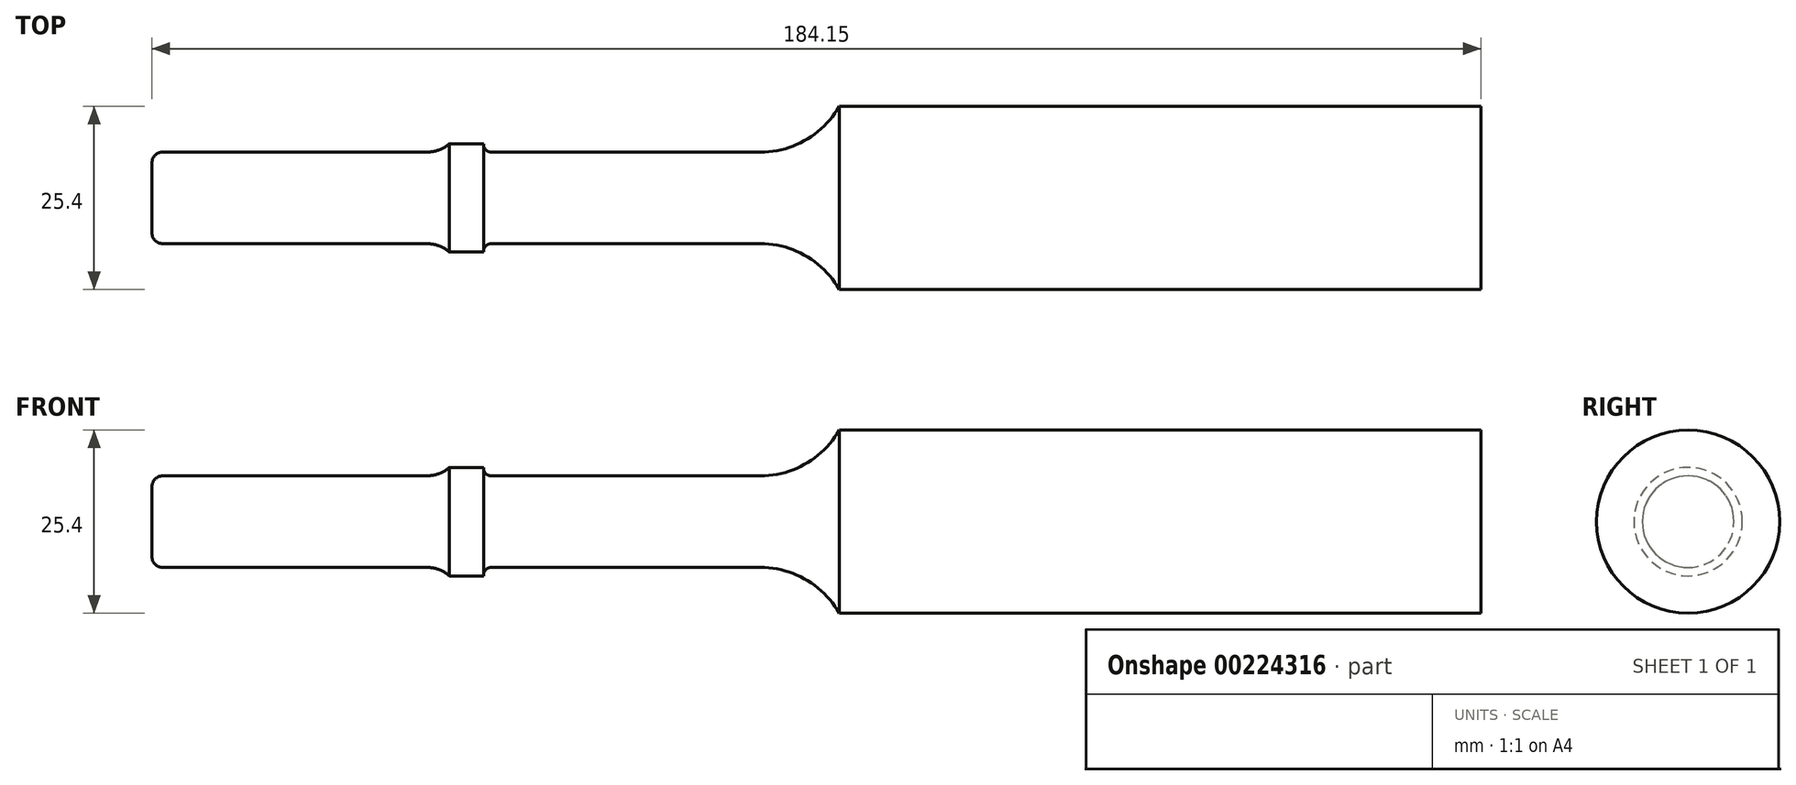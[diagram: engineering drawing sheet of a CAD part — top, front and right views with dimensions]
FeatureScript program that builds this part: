
annotation { "Feature Type Name" : "Feature", "Feature Type Description" : "" }
export const myFeature = defineFeature(function(context is Context, id is Id, definition is map)
    precondition{}
    {
        {
            var Q0;
            Q0=qCreatedBy(makeId("Front.planeOp"),FACE);
            var sketch = newSketch(context, id + "F0", { "sketchPlane" : qUnion([Q0])});
            skLineSegment(sketch, "E0", {"start": v(0, 0) * mm, "end": v(0, -6.35) * mm});
            skLineSegment(sketch, "E1", {"start": v(0, -6.35) * mm, "end": v(184.15, -6.35) * mm});
            skLineSegment(sketch, "E2", {"start": v(184.15, -6.35) * mm, "end": v(184.15, 6.35) * mm});
            skLineSegment(sketch, "E3", {"start": v(184.15, 6.35) * mm, "end": v(95.25, 6.35) * mm});
            skLineSegment(sketch, "E4", {"start": v(0, 0) * mm, "end": v(38.1, 0) * mm});
            skArc(sketch, "E5", {"start": v(38.1, 0) * mm, "mid": v(39.77, 0.3) * mm, "end": v(41.22, 1.17) * mm});
            skLineSegment(sketch, "E6", {"start": v(41.22, 1.17) * mm, "end": v(45.97, 1.17) * mm});
            skLineSegment(sketch, "E7", {"start": v(47, 0) * mm, "end": v(84.3, 0) * mm});
            skArc(sketch, "E8", {"start": v(84.3, 0) * mm, "mid": v(90.63, 1.7) * mm, "end": v(95.25, 6.35) * mm});
            skArc(sketch, "E9", {"start": v(47, 0) * mm, "mid": v(46.22, 0.35) * mm, "end": v(45.97, 1.17) * mm});
            skSolve(sketch);
        }
        {
            var Q0;
            Q0=makeQuery(id+"F0.imprint","IMPRINT",FACE,{"disambiguationData":[TD([[makeQuery(id+"F0.imprint","IMPRINT",EDGE,{"derivedFrom":sQuery(id+"F0.wireOp",EDGE,"E0")}),1.0]])]});
            var Q1;
            Q1=sQuery(id+"F0.wireOp",EDGE,"E1");
            revolve(context, id + "F1", {"entities" : qUnion([Q0]), "axis" : qUnion([Q1]), "revolveType" : RevolveType.FULL});
        }
        {
            var Q0;
            Q0=makeQuery(id+"F1.opRevolve","SWEPT_EDGE",EDGE,{"disambiguationData":[OSD([sQuery(id+"F0.wireOp",EDGE,"E0"),sQuery(id+"F0.wireOp",EDGE,"E4")])]});
            fillet(context, id + "F2", {"entities" : qUnion([Q0]), "radius" : 1.52 * mm, "tangentPropagation" : true, "allowEdgeOverflow" : false});
        }
    });
